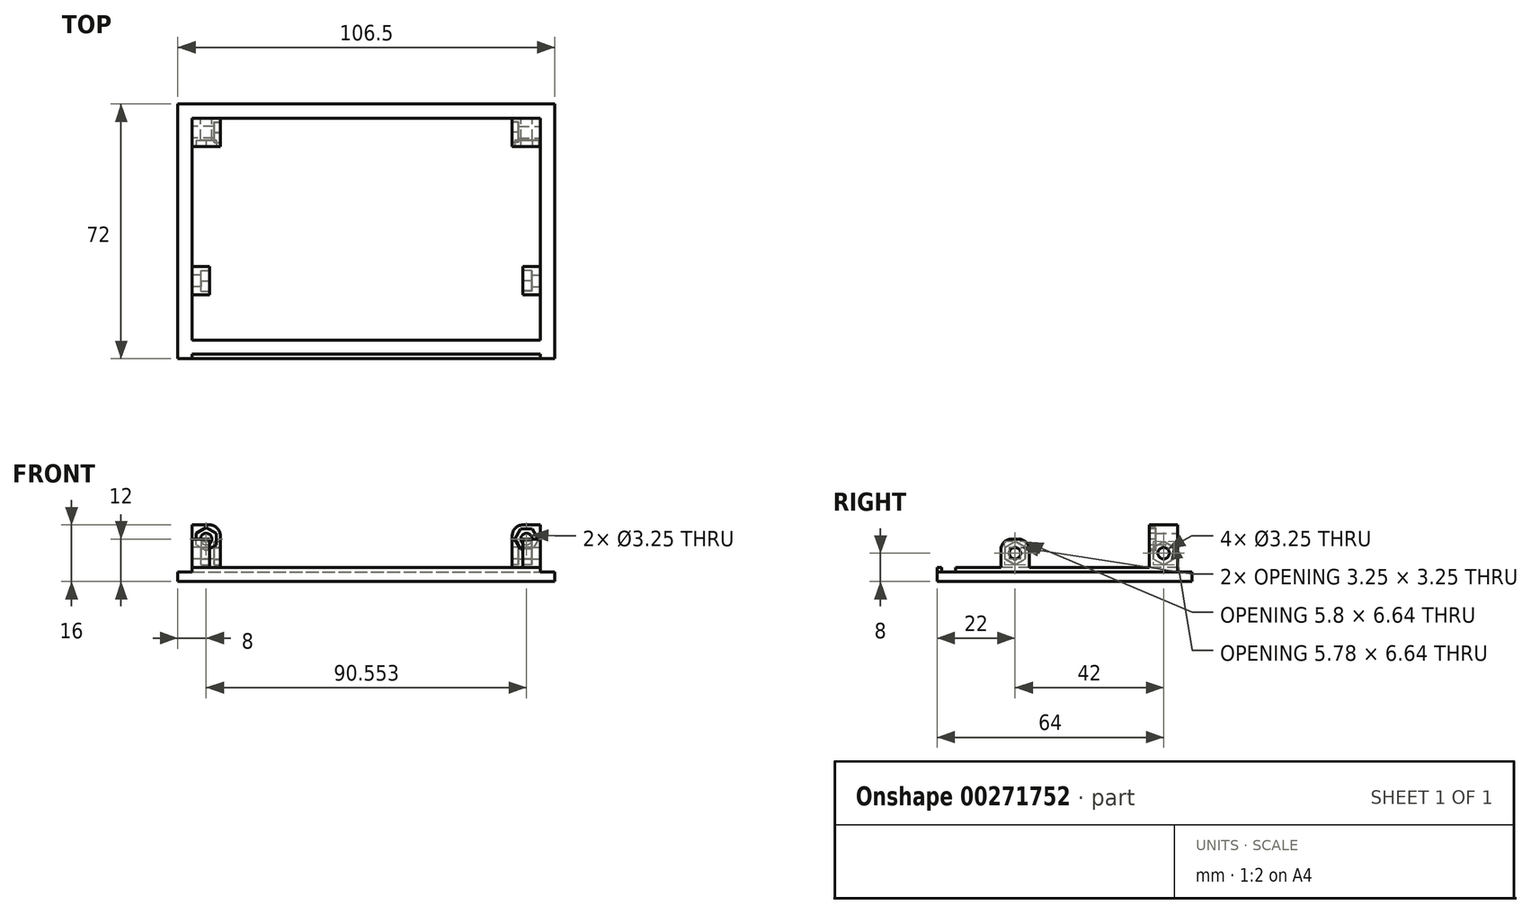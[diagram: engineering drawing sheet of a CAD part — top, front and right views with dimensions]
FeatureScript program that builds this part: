
annotation { "Feature Type Name" : "Feature", "Feature Type Description" : "" }
export const myFeature = defineFeature(function(context is Context, id is Id, definition is map)
    precondition{}
    {
        {
            var Q0;
            Q0=qCreatedBy(makeId("Top.planeOp"),FACE);
            var sketch = newSketch(context, id + "F0", { "sketchPlane" : qUnion([Q0])});
            skLineSegment(sketch, "E0.bottom", {"start": v(-53.25, 36) * mm, "end": v(53.25, 36) * mm});
            skLineSegment(sketch, "E0.top", {"start": v(-53.25, -36) * mm, "end": v(53.25, -36) * mm});
            skLineSegment(sketch, "E0.left", {"start": v(-53.25, 36) * mm, "end": v(-53.25, -36) * mm});
            skLineSegment(sketch, "E0.right", {"start": v(53.25, 36) * mm, "end": v(53.25, -36) * mm});
            skSolve(sketch);
        }
        {
            var Q0;
            Q0 = qSketchRegion(id + "F0", true);
            extrude(context, id + "F1", {"entities" : qUnion([Q0]), "depth" : 2.75 * mm});
        }
        {
            var Q0;
            Q0=makeQuery(id+"F1.opExtrude","CAP_FACE",FACE,{"disambiguationData":[OSD([sQuery(id+"F0.wireOp",EDGE,"E0.bottom"),sQuery(id+"F0.wireOp",EDGE,"E0.top"),sQuery(id+"F0.wireOp",EDGE,"E0.left"),sQuery(id+"F0.wireOp",EDGE,"E0.right")])],"isStart":false});
            var sketch = newSketch(context, id + "F2", { "sketchPlane" : qUnion([Q0])});
            skLineSegment(sketch, "E1.bottom", {"start": v(-49.25, 32) * mm, "end": v(49.25, 32) * mm});
            skLineSegment(sketch, "E1.top", {"start": v(-49.25, -30.75) * mm, "end": v(49.25, -30.75) * mm});
            skLineSegment(sketch, "E1.left", {"start": v(-49.25, 32) * mm, "end": v(-49.25, -30.75) * mm});
            skLineSegment(sketch, "E1.right", {"start": v(49.25, 32) * mm, "end": v(49.25, -30.75) * mm});
            skLineSegment(sketch, "E2.bottom", {"start": v(-49.25, -36) * mm, "end": v(49.25, -36) * mm});
            skLineSegment(sketch, "E2.top", {"start": v(-49.25, -34.75) * mm, "end": v(49.25, -34.75) * mm});
            skLineSegment(sketch, "E2.left", {"start": v(-49.25, -36) * mm, "end": v(-49.25, -34.75) * mm});
            skLineSegment(sketch, "E2.right", {"start": v(49.25, -36) * mm, "end": v(49.25, -34.75) * mm});
            skSolve(sketch);
        }
        {
            var Q0;
            Q0 = qSketchRegion(id + "F2", true);
            extrude(context, id + "F3", {"entities" : qUnion([Q0]), "operationType" : NewBodyOperationType.ADD, "depth" : 1.25 * mm});
        }
        {
            var Q0;
            Q0=makeQuery(id+"F3.opExtrude","CAP_FACE",FACE,{"disambiguationData":[OSD([sQuery(id+"F2.wireOp",EDGE,"E1.bottom"),sQuery(id+"F2.wireOp",EDGE,"E1.top"),sQuery(id+"F2.wireOp",EDGE,"E1.left"),sQuery(id+"F2.wireOp",EDGE,"E1.right")])],"isStart":false});
            var sketch = newSketch(context, id + "F4", { "sketchPlane" : qUnion([Q0])});
            skLineSegment(sketch, "E3.bottom", {"start": v(-49.25, 32) * mm, "end": v(-41.25, 32) * mm});
            skLineSegment(sketch, "E3.top", {"start": v(-49.25, 24) * mm, "end": v(-41.25, 24) * mm});
            skLineSegment(sketch, "E3.left", {"start": v(-49.25, 32) * mm, "end": v(-49.25, 24) * mm});
            skLineSegment(sketch, "E3.right", {"start": v(-41.25, 32) * mm, "end": v(-41.25, 24) * mm});
            skLineSegment(sketch, "E4.bottom", {"start": v(49.25, 32) * mm, "end": v(41.25, 32) * mm});
            skLineSegment(sketch, "E4.top", {"start": v(49.25, 24) * mm, "end": v(41.25, 24) * mm});
            skLineSegment(sketch, "E4.left", {"start": v(49.25, 32) * mm, "end": v(49.25, 24) * mm});
            skLineSegment(sketch, "E4.right", {"start": v(41.25, 32) * mm, "end": v(41.25, 24) * mm});
            skSolve(sketch);
        }
        {
            var Q0;
            Q0 = qSketchRegion(id + "F4", true);
            extrude(context, id + "F5", {"entities" : qUnion([Q0]), "operationType" : NewBodyOperationType.ADD, "depth" : 12 * mm});
        }
        {
            var Q0;
            Q0=makeQuery(id+"F3.opExtrude","CAP_FACE",FACE,{"disambiguationData":[OSD([sQuery(id+"F2.wireOp",EDGE,"E1.bottom"),sQuery(id+"F2.wireOp",EDGE,"E1.top"),sQuery(id+"F2.wireOp",EDGE,"E1.left"),sQuery(id+"F2.wireOp",EDGE,"E1.right")])],"isStart":false});
            var sketch = newSketch(context, id + "F6", { "sketchPlane" : qUnion([Q0])});
            skLineSegment(sketch, "E5.bottom", {"start": v(-49.25, -10) * mm, "end": v(-44.25, -10) * mm});
            skLineSegment(sketch, "E5.top", {"start": v(-49.25, -18) * mm, "end": v(-44.25, -18) * mm});
            skLineSegment(sketch, "E5.left", {"start": v(-49.25, -10) * mm, "end": v(-49.25, -18) * mm});
            skLineSegment(sketch, "E5.right", {"start": v(-44.25, -10) * mm, "end": v(-44.25, -18) * mm});
            skLineSegment(sketch, "E6.bottom", {"start": v(49.25, -10) * mm, "end": v(44.25, -10) * mm});
            skLineSegment(sketch, "E6.top", {"start": v(49.25, -18) * mm, "end": v(44.25, -18) * mm});
            skLineSegment(sketch, "E6.left", {"start": v(49.25, -10) * mm, "end": v(49.25, -18) * mm});
            skLineSegment(sketch, "E6.right", {"start": v(44.25, -10) * mm, "end": v(44.25, -18) * mm});
            skSolve(sketch);
        }
        {
            var Q0;
            Q0 = qSketchRegion(id + "F6", true);
            extrude(context, id + "F7", {"entities" : qUnion([Q0]), "operationType" : NewBodyOperationType.ADD, "depth" : 8 * mm});
        }
        {
            var Q0;
            Q0=makeQuery(id+"F7.boolean.opBoolean","MERGE",FACE,{"derivedFrom":[makeQuery(id+"F5.boolean.opBoolean","MERGE",FACE,{"derivedFrom":[makeQuery(id+"F3.opExtrude","SWEPT_FACE",FACE,{"disambiguationData":[OSD([sQuery(id+"F2.wireOp",EDGE,"E1.left")])]}),makeQuery(id+"F5.opExtrude","SWEPT_FACE",FACE,{"disambiguationData":[OSD([sQuery(id+"F4.wireOp",EDGE,"E3.left")])]})]}),makeQuery(id+"F7.opExtrude","SWEPT_FACE",FACE,{"disambiguationData":[OSD([sQuery(id+"F6.wireOp",EDGE,"E5.left")])]})]});
            var sketch = newSketch(context, id + "F8", { "sketchPlane" : qUnion([Q0])});
            skPoint(sketch, "E7", {"position": v(-28, 8) * mm});
            skPoint(sketch, "E8", {"position": v(14, 8) * mm});
            skSolve(sketch);
        }
        {
            var Q0;
            Q0=makeQuery(id+"F7.boolean.opBoolean","MERGE",FACE,{"derivedFrom":[makeQuery(id+"F5.boolean.opBoolean","MERGE",FACE,{"derivedFrom":[makeQuery(id+"F3.opExtrude","SWEPT_FACE",FACE,{"disambiguationData":[OSD([sQuery(id+"F2.wireOp",EDGE,"E1.right")])]}),makeQuery(id+"F5.opExtrude","SWEPT_FACE",FACE,{"disambiguationData":[OSD([sQuery(id+"F4.wireOp",EDGE,"E4.left")])]})]}),makeQuery(id+"F7.opExtrude","SWEPT_FACE",FACE,{"disambiguationData":[OSD([sQuery(id+"F6.wireOp",EDGE,"E6.left")])]})]});
            var sketch = newSketch(context, id + "F9", { "sketchPlane" : qUnion([Q0])});
            skPoint(sketch, "E9", {"position": v(-14, 8) * mm});
            skPoint(sketch, "E10", {"position": v(28, 8) * mm});
            skSolve(sketch);
        }
        {
            var Q0;
            Q0=makeQuery(id+"F5.boolean.opBoolean","MERGE",FACE,{"derivedFrom":[makeQuery(id+"F3.opExtrude","SWEPT_FACE",FACE,{"disambiguationData":[OSD([sQuery(id+"F2.wireOp",EDGE,"E1.bottom")])]}),makeQuery(id+"F5.opExtrude","SWEPT_FACE",FACE,{"disambiguationData":[OSD([sQuery(id+"F4.wireOp",EDGE,"E3.bottom")])]}),makeQuery(id+"F5.opExtrude","SWEPT_FACE",FACE,{"disambiguationData":[OSD([sQuery(id+"F4.wireOp",EDGE,"E4.bottom")])]})]});
            var sketch = newSketch(context, id + "F10", { "sketchPlane" : qUnion([Q0])});
            skPoint(sketch, "E11", {"position": v(-45.3, 12) * mm});
            skPoint(sketch, "E12", {"position": v(45.25, 12) * mm});
            skSolve(sketch);
        }
        {
            var Q0;
            Q0=sQuery(id+"F10.wireOp",VERTEX,"E11");
            var Q1;
            Q1=sQuery(id+"F10.wireOp",VERTEX,"E12");
            var Q2;
            Q2=makeQuery(id+"F1.opExtrude","SWEPT_BODY",BODY,{"disambiguationData":[OSD([sQuery(id+"F0.wireOp",EDGE,"E0.bottom"),sQuery(id+"F0.wireOp",EDGE,"E0.top"),sQuery(id+"F0.wireOp",EDGE,"E0.left"),sQuery(id+"F0.wireOp",EDGE,"E0.right")])]});
            hole(context, id + "F11", {"style" : HoleStyle.SIMPLE, "endStyle" : HoleEndStyle.BLIND, "holeDiameter" : 3.25 * mm, "holeDepth" : 8 * mm, "tappedDepth" : 12 * mm, "tapClearance" : 3, "startFromSketch" : true, "locations" : qUnion([Q0, Q1]), "scope" : qUnion([Q2])});
        }
        {
            var Q0;
            Q0=sQuery(id+"F8.wireOp",VERTEX,"E7");
            var Q1;
            Q1=sQuery(id+"F8.wireOp",VERTEX,"E8");
            var Q2;
            Q2=makeQuery(id+"F1.opExtrude","SWEPT_BODY",BODY,{"disambiguationData":[OSD([sQuery(id+"F0.wireOp",EDGE,"E0.bottom"),sQuery(id+"F0.wireOp",EDGE,"E0.top"),sQuery(id+"F0.wireOp",EDGE,"E0.left"),sQuery(id+"F0.wireOp",EDGE,"E0.right")])]});
            hole(context, id + "F12", {"style" : HoleStyle.SIMPLE, "endStyle" : HoleEndStyle.BLIND, "holeDiameter" : 3.25 * mm, "holeDepth" : 8 * mm, "tappedDepth" : 12 * mm, "tapClearance" : 3, "startFromSketch" : true, "locations" : qUnion([Q0, Q1]), "scope" : qUnion([Q2])});
        }
        {
            var Q0;
            Q0=sQuery(id+"F9.wireOp",VERTEX,"E9");
            var Q1;
            Q1=sQuery(id+"F9.wireOp",VERTEX,"E10");
            var Q2;
            Q2=makeQuery(id+"F1.opExtrude","SWEPT_BODY",BODY,{"disambiguationData":[OSD([sQuery(id+"F0.wireOp",EDGE,"E0.bottom"),sQuery(id+"F0.wireOp",EDGE,"E0.top"),sQuery(id+"F0.wireOp",EDGE,"E0.left"),sQuery(id+"F0.wireOp",EDGE,"E0.right")])]});
            hole(context, id + "F13", {"style" : HoleStyle.SIMPLE, "endStyle" : HoleEndStyle.BLIND, "holeDiameter" : 3.25 * mm, "holeDepth" : 8 * mm, "tappedDepth" : 12 * mm, "tapClearance" : 3, "startFromSketch" : true, "locations" : qUnion([Q0, Q1]), "scope" : qUnion([Q2])});
        }
        {
            var Q0;
            Q0=makeQuery(id+"F7.opExtrude","SWEPT_FACE",FACE,{"disambiguationData":[OSD([sQuery(id+"F6.wireOp",EDGE,"E5.right")])]});
            var sketch = newSketch(context, id + "F14", { "sketchPlane" : qUnion([Q0])});
            skCircle(sketch, "E13.cCircle", {"center": v(-14, 8) * mm, "radius": 2.88 * mm, "construction": true});
            skLineSegment(sketch, "E13.0", {"start": v(-11.12, 9.66) * mm, "end": v(-11.12, 6.34) * mm});
            skLineSegment(sketch, "E13.1", {"start": v(-11.12, 6.34) * mm, "end": v(-14, 4.68) * mm});
            skLineSegment(sketch, "E13.2", {"start": v(-14, 4.68) * mm, "end": v(-16.87, 6.34) * mm});
            skLineSegment(sketch, "E13.3", {"start": v(-16.87, 6.34) * mm, "end": v(-16.87, 9.66) * mm});
            skLineSegment(sketch, "E13.4", {"start": v(-16.87, 9.66) * mm, "end": v(-14, 11.32) * mm});
            skLineSegment(sketch, "E13.5", {"start": v(-14, 11.32) * mm, "end": v(-11.12, 9.66) * mm});
            skPoint(sketch, "E13.0.midPoint", {"position": v(-11.12, 8) * mm});
            skSolve(sketch);
        }
        {
            var Q0;
            Q0 = qSketchRegion(id + "F14", true);
            extrude(context, id + "F15", {"entities" : qUnion([Q0]), "operationType" : NewBodyOperationType.REMOVE, "oppositeDirection" : true, "depth" : 2.5 * mm});
        }
        {
            var Q0;
            Q0=makeQuery(id+"F5.opExtrude","SWEPT_FACE",FACE,{"disambiguationData":[OSD([sQuery(id+"F4.wireOp",EDGE,"E3.right")])]});
            var sketch = newSketch(context, id + "F16", { "sketchPlane" : qUnion([Q0])});
            skCircle(sketch, "E14.cCircle", {"center": v(28, 8) * mm, "radius": 2.88 * mm, "construction": true});
            skLineSegment(sketch, "E14.0", {"start": v(27.94, 11.32) * mm, "end": v(30.84, 9.71) * mm});
            skLineSegment(sketch, "E14.1", {"start": v(30.84, 9.71) * mm, "end": v(30.9, 6.4) * mm});
            skLineSegment(sketch, "E14.2", {"start": v(30.9, 6.4) * mm, "end": v(28.06, 4.68) * mm});
            skLineSegment(sketch, "E14.3", {"start": v(28.06, 4.68) * mm, "end": v(25.16, 6.29) * mm});
            skLineSegment(sketch, "E14.4", {"start": v(25.16, 6.29) * mm, "end": v(25.1, 9.6) * mm});
            skLineSegment(sketch, "E14.5", {"start": v(25.1, 9.6) * mm, "end": v(27.94, 11.32) * mm});
            skPoint(sketch, "E14.0.midPoint", {"position": v(29.4, 10.52) * mm});
            skSolve(sketch);
        }
        {
            var Q0;
            Q0 = qSketchRegion(id + "F16", true);
            extrude(context, id + "F17", {"entities" : qUnion([Q0]), "operationType" : NewBodyOperationType.REMOVE, "oppositeDirection" : true, "depth" : 1.75 * mm});
        }
        {
            var Q0;
            Q0=makeQuery(id+"F5.opExtrude","SWEPT_FACE",FACE,{"disambiguationData":[OSD([sQuery(id+"F4.wireOp",EDGE,"E4.right")])]});
            var sketch = newSketch(context, id + "F18", { "sketchPlane" : qUnion([Q0])});
            skCircle(sketch, "E15.cCircle", {"center": v(-28, 8) * mm, "radius": 2.88 * mm, "construction": true});
            skLineSegment(sketch, "E15.0", {"start": v(-27.97, 11.32) * mm, "end": v(-25.1, 9.63) * mm});
            skLineSegment(sketch, "E15.1", {"start": v(-25.1, 9.63) * mm, "end": v(-25.14, 6.31) * mm});
            skLineSegment(sketch, "E15.2", {"start": v(-25.14, 6.31) * mm, "end": v(-28.03, 4.68) * mm});
            skLineSegment(sketch, "E15.3", {"start": v(-28.03, 4.68) * mm, "end": v(-30.9, 6.37) * mm});
            skLineSegment(sketch, "E15.4", {"start": v(-30.9, 6.37) * mm, "end": v(-30.86, 9.69) * mm});
            skLineSegment(sketch, "E15.5", {"start": v(-30.86, 9.69) * mm, "end": v(-27.97, 11.32) * mm});
            skPoint(sketch, "E15.0.midPoint", {"position": v(-26.54, 10.48) * mm});
            skSolve(sketch);
        }
        {
            var Q0;
            Q0 = qSketchRegion(id + "F18", true);
            extrude(context, id + "F19", {"entities" : qUnion([Q0]), "operationType" : NewBodyOperationType.REMOVE, "oppositeDirection" : true, "depth" : 1.75 * mm});
        }
        {
            var Q0;
            Q0=makeQuery(id+"F7.opExtrude","SWEPT_FACE",FACE,{"disambiguationData":[OSD([sQuery(id+"F6.wireOp",EDGE,"E6.right")])]});
            var sketch = newSketch(context, id + "F20", { "sketchPlane" : qUnion([Q0])});
            skCircle(sketch, "E16.cCircle", {"center": v(14, 8) * mm, "radius": 2.88 * mm, "construction": true});
            skLineSegment(sketch, "E16.0", {"start": v(11.1, 9.62) * mm, "end": v(13.95, 11.32) * mm});
            skLineSegment(sketch, "E16.1", {"start": v(13.95, 11.32) * mm, "end": v(16.85, 9.7) * mm});
            skLineSegment(sketch, "E16.2", {"start": v(16.85, 9.7) * mm, "end": v(16.9, 6.38) * mm});
            skLineSegment(sketch, "E16.3", {"start": v(16.9, 6.38) * mm, "end": v(14.05, 4.68) * mm});
            skLineSegment(sketch, "E16.4", {"start": v(14.05, 4.68) * mm, "end": v(11.15, 6.3) * mm});
            skLineSegment(sketch, "E16.5", {"start": v(11.15, 6.3) * mm, "end": v(11.1, 9.62) * mm});
            skPoint(sketch, "E16.0.midPoint", {"position": v(12.53, 10.47) * mm});
            skSolve(sketch);
        }
        {
            var Q0;
            Q0 = qSketchRegion(id + "F20", true);
            extrude(context, id + "F21", {"entities" : qUnion([Q0]), "operationType" : NewBodyOperationType.REMOVE, "oppositeDirection" : true, "depth" : 2.5 * mm});
        }
        {
            var Q0;
            Q0=makeQuery(id+"F5.opExtrude","SWEPT_FACE",FACE,{"disambiguationData":[OSD([sQuery(id+"F4.wireOp",EDGE,"E3.top")])]});
            var sketch = newSketch(context, id + "F22", { "sketchPlane" : qUnion([Q0])});
            skCircle(sketch, "E17.cCircle", {"center": v(-45.25, 12) * mm, "radius": 2.88 * mm, "construction": true});
            skLineSegment(sketch, "E17.0", {"start": v(-42.38, 13.66) * mm, "end": v(-42.38, 10.34) * mm});
            skLineSegment(sketch, "E17.1", {"start": v(-42.38, 10.34) * mm, "end": v(-45.25, 8.68) * mm});
            skLineSegment(sketch, "E17.2", {"start": v(-45.25, 8.68) * mm, "end": v(-48.12, 10.34) * mm});
            skLineSegment(sketch, "E17.3", {"start": v(-48.12, 10.34) * mm, "end": v(-48.12, 13.66) * mm});
            skLineSegment(sketch, "E17.4", {"start": v(-48.12, 13.66) * mm, "end": v(-45.25, 15.32) * mm});
            skLineSegment(sketch, "E17.5", {"start": v(-45.25, 15.32) * mm, "end": v(-42.38, 13.66) * mm});
            skPoint(sketch, "E17.0.midPoint", {"position": v(-42.38, 12) * mm});
            skSolve(sketch);
        }
        {
            var Q0;
            Q0 = qSketchRegion(id + "F22", true);
            extrude(context, id + "F23", {"entities" : qUnion([Q0]), "operationType" : NewBodyOperationType.REMOVE, "oppositeDirection" : true, "depth" : 1.75 * mm});
        }
        {
            var Q0;
            Q0=makeQuery(id+"F5.opExtrude","SWEPT_FACE",FACE,{"disambiguationData":[OSD([sQuery(id+"F4.wireOp",EDGE,"E4.top")])]});
            var sketch = newSketch(context, id + "F24", { "sketchPlane" : qUnion([Q0])});
            skCircle(sketch, "E18.cCircle", {"center": v(45.3, 12) * mm, "radius": 2.88 * mm, "construction": true});
            skLineSegment(sketch, "E18.0", {"start": v(43.63, 9.13) * mm, "end": v(41.98, 12.01) * mm});
            skLineSegment(sketch, "E18.1", {"start": v(41.98, 12.01) * mm, "end": v(43.65, 14.88) * mm});
            skLineSegment(sketch, "E18.2", {"start": v(43.65, 14.88) * mm, "end": v(46.97, 14.87) * mm});
            skLineSegment(sketch, "E18.3", {"start": v(46.97, 14.87) * mm, "end": v(48.62, 11.99) * mm});
            skLineSegment(sketch, "E18.4", {"start": v(48.62, 11.99) * mm, "end": v(46.95, 9.12) * mm});
            skLineSegment(sketch, "E18.5", {"start": v(46.95, 9.12) * mm, "end": v(43.63, 9.13) * mm});
            skPoint(sketch, "E18.0.midPoint", {"position": v(42.8, 10.57) * mm});
            skSolve(sketch);
        }
        {
            var Q0;
            Q0 = qSketchRegion(id + "F24", true);
            extrude(context, id + "F25", {"entities" : qUnion([Q0]), "operationType" : NewBodyOperationType.REMOVE, "oppositeDirection" : true, "depth" : 1.75 * mm});
        }
        {
            var Q0;
            Q0=makeQuery(id+"F7.opExtrude","CAP_EDGE",EDGE,{"disambiguationData":[OSD([sQuery(id+"F6.wireOp",EDGE,"E6.top")])],"isStart":false});
            var Q1;
            Q1=makeQuery(id+"F7.opExtrude","CAP_EDGE",EDGE,{"disambiguationData":[OSD([sQuery(id+"F6.wireOp",EDGE,"E6.bottom")])],"isStart":false});
            var Q2;
            Q2=makeQuery(id+"F7.opExtrude","CAP_EDGE",EDGE,{"disambiguationData":[OSD([sQuery(id+"F6.wireOp",EDGE,"E5.top")])],"isStart":false});
            var Q3;
            Q3=makeQuery(id+"F7.opExtrude","CAP_EDGE",EDGE,{"disambiguationData":[OSD([sQuery(id+"F6.wireOp",EDGE,"E5.bottom")])],"isStart":false});
            var Q4;
            Q4=makeQuery(id+"F5.opExtrude","CAP_EDGE",EDGE,{"disambiguationData":[OSD([sQuery(id+"F4.wireOp",EDGE,"E3.right")])],"isStart":false});
            var Q5;
            Q5=makeQuery(id+"F5.opExtrude","CAP_EDGE",EDGE,{"disambiguationData":[OSD([sQuery(id+"F4.wireOp",EDGE,"E4.right")])],"isStart":false});
            fillet(context, id + "F26", {"entities" : qUnion([Q0, Q1, Q2, Q3, Q4, Q5]), "radius" : 3 * mm, "tangentPropagation" : true, "allowEdgeOverflow" : false});
        }
    });
